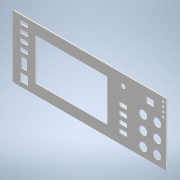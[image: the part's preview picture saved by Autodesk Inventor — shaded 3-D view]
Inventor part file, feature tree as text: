
AUTODESK INVENTOR PART (.ipt)
format: ipt  version: 2020.3 (Build 243373000, 373)  size: 306,688 bytes
history: native  units: mm
features: fillet x3, extrude x1, sketch x1
ambient origin geometry x8: Origin, YZ Plane, XZ Plane, XY Plane, X Axis, Y Axis, Z Axis, Center Point
bodies: Body1 (feature_tree)
feature tree (5):
  extrude  "Extrusion2"  Depth=84.0mm
  fillet  "Fillet1"  Radius=56.4mm
  fillet  "Fillet2"  Radius=97.22mm
  fillet  "Fillet3"  Radius=10.6mm
  sketch  "Sketch1"  dims[d0=207.0mm d1=84.0mm d4=56.4mm d5=97.22mm d6=10.6mm d7=10.0mm d8=6.0mm d9=19.0mm d10=19.0mm d11=11.0mm d12=19.0mm d13=95.04mm d14=53.86mm d15=5.19mm d16=3.98mm d17=67.07mm d18=105.42mm d21=10.0mm d22=12.0mm d23=12.0mm d24=13.9mm d25=7.5mm d26=5.5mm d27=5.0mm d28=5.5mm d29=5.5mm d30=5.5mm d31=5.5mm d32=10.0mm d33=6.0mm d34=22.0mm d35=10.0mm d36=8.0mm d37=3.2mm d38=3.2mm d39=3.2mm d40=3.2mm d41=6.0mm d42=6.0mm d43=6.0mm d44=4.0mm d45=5.0mm d46=5.5mm d47=5.5mm d48=5.5mm d49=10.0mm d50=5.5mm d51=5.5mm d52=6.0mm d53=1.6mm d54=0.0mm d55=1.0mm d56=0.75mm d57=0.5mm]
